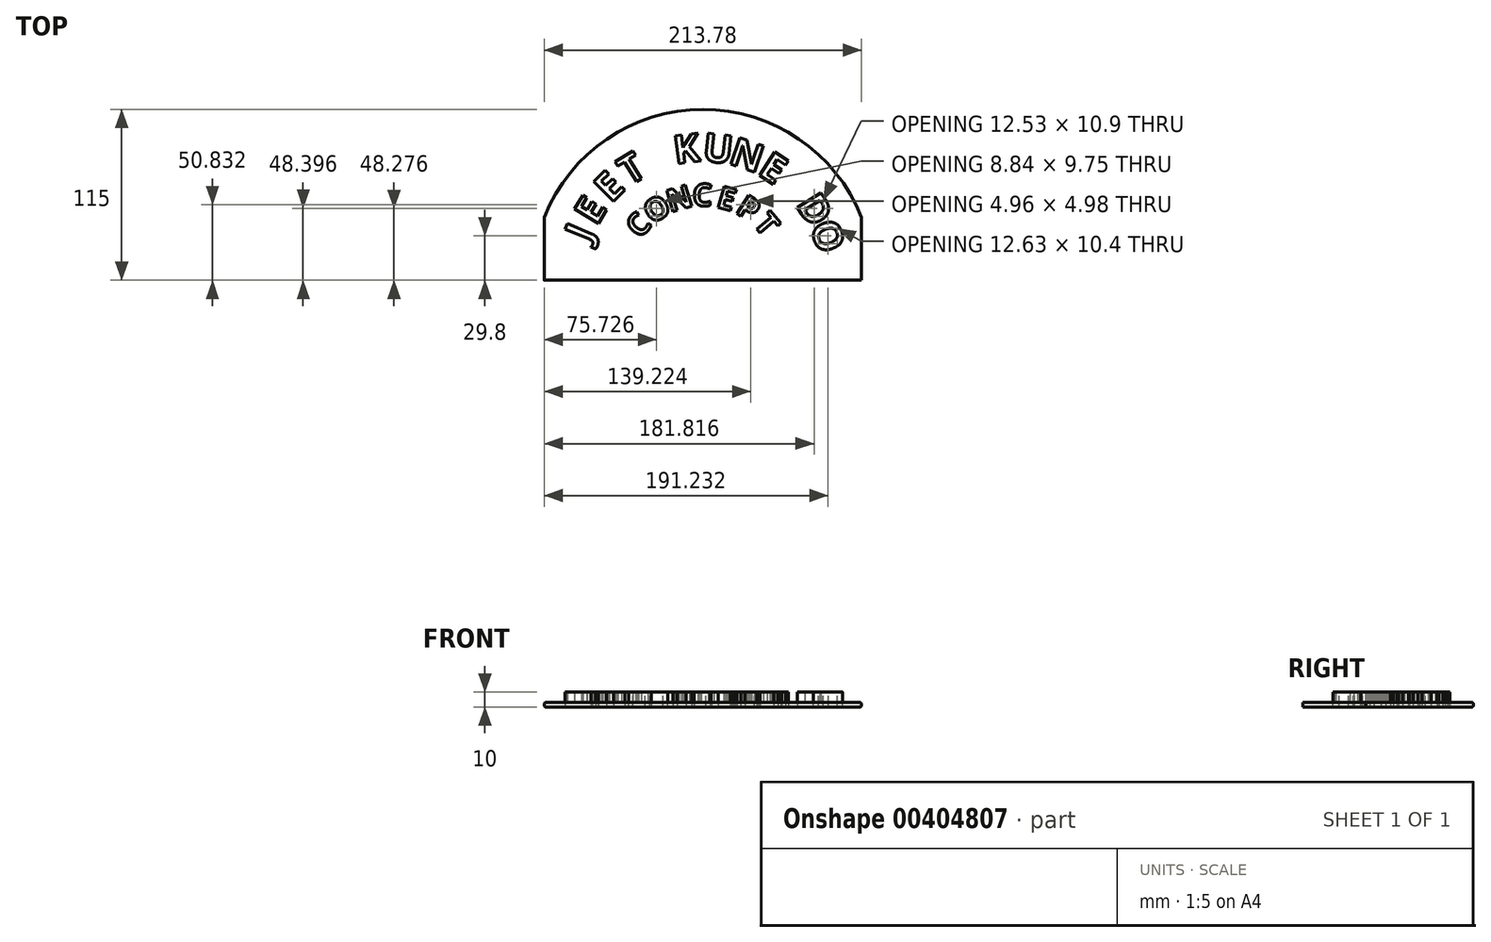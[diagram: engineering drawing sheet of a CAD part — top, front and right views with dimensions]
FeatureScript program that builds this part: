
annotation { "Feature Type Name" : "Feature", "Feature Type Description" : "" }
export const myFeature = defineFeature(function(context is Context, id is Id, definition is map)
    precondition{}
    {
        {
            var Q0;
            Q0=qCreatedBy(makeId("Top.planeOp"),FACE);
            var sketch = newSketch(context, id + "F0", { "sketchPlane" : qUnion([Q0])});
            skCircle(sketch, "E0.cCircle", {"center": v(0, 0) * mm, "radius": 80 * mm, "construction": true});
            skLineSegment(sketch, "E0.0", {"start": v(80.5, 0) * mm, "end": v(78.49, -17.91) * mm, "construction": true});
            skLineSegment(sketch, "E0.1", {"start": v(78.49, -17.91) * mm, "end": v(72.53, -34.93) * mm, "construction": true});
            skLineSegment(sketch, "E0.2", {"start": v(72.53, -34.93) * mm, "end": v(62.94, -50.2) * mm, "construction": true});
            skLineSegment(sketch, "E0.3", {"start": v(62.94, -50.2) * mm, "end": v(50.2, -62.94) * mm, "construction": true});
            skLineSegment(sketch, "E0.4", {"start": v(50.2, -62.94) * mm, "end": v(34.93, -72.53) * mm, "construction": true});
            skLineSegment(sketch, "E0.5", {"start": v(34.93, -72.53) * mm, "end": v(17.91, -78.49) * mm, "construction": true});
            skLineSegment(sketch, "E0.6", {"start": v(17.91, -78.49) * mm, "end": v(0, -80.5) * mm, "construction": true});
            skLineSegment(sketch, "E0.7", {"start": v(0, -80.5) * mm, "end": v(-17.91, -78.49) * mm, "construction": true});
            skLineSegment(sketch, "E0.8", {"start": v(-17.91, -78.49) * mm, "end": v(-34.93, -72.53) * mm, "construction": true});
            skLineSegment(sketch, "E0.9", {"start": v(-34.93, -72.53) * mm, "end": v(-50.2, -62.94) * mm, "construction": true});
            skLineSegment(sketch, "E0.10", {"start": v(-50.2, -62.94) * mm, "end": v(-62.94, -50.2) * mm, "construction": true});
            skLineSegment(sketch, "E0.11", {"start": v(-62.94, -50.2) * mm, "end": v(-72.53, -34.93) * mm, "construction": true});
            skLineSegment(sketch, "E0.12", {"start": v(-72.53, -34.93) * mm, "end": v(-78.49, -17.91) * mm, "construction": true});
            skLineSegment(sketch, "E0.13", {"start": v(-78.49, -17.91) * mm, "end": v(-80.5, 0) * mm, "construction": true});
            skLineSegment(sketch, "E0.14", {"start": v(-80.5, 0) * mm, "end": v(-78.49, 17.91) * mm, "construction": true});
            skLineSegment(sketch, "E0.15", {"start": v(-78.49, 17.91) * mm, "end": v(-72.53, 34.93) * mm, "construction": true});
            skLineSegment(sketch, "E0.16", {"start": v(-72.53, 34.93) * mm, "end": v(-62.94, 50.2) * mm, "construction": true});
            skLineSegment(sketch, "E0.17", {"start": v(-62.94, 50.2) * mm, "end": v(-50.2, 62.94) * mm, "construction": true});
            skLineSegment(sketch, "E0.18", {"start": v(-50.2, 62.94) * mm, "end": v(-34.93, 72.53) * mm, "construction": true});
            skLineSegment(sketch, "E0.19", {"start": v(-34.93, 72.53) * mm, "end": v(-17.91, 78.49) * mm, "construction": true});
            skLineSegment(sketch, "E0.20", {"start": v(-17.91, 78.49) * mm, "end": v(0, 80.5) * mm, "construction": true});
            skLineSegment(sketch, "E0.21", {"start": v(0, 80.5) * mm, "end": v(17.91, 78.49) * mm, "construction": true});
            skLineSegment(sketch, "E0.22", {"start": v(17.91, 78.49) * mm, "end": v(34.93, 72.53) * mm, "construction": true});
            skLineSegment(sketch, "E0.23", {"start": v(34.93, 72.53) * mm, "end": v(50.2, 62.94) * mm, "construction": true});
            skLineSegment(sketch, "E0.24", {"start": v(50.2, 62.94) * mm, "end": v(62.94, 50.2) * mm, "construction": true});
            skLineSegment(sketch, "E0.25", {"start": v(62.94, 50.2) * mm, "end": v(72.53, 34.93) * mm, "construction": true});
            skLineSegment(sketch, "E0.26", {"start": v(72.53, 34.93) * mm, "end": v(78.49, 17.91) * mm, "construction": true});
            skLineSegment(sketch, "E0.27", {"start": v(78.49, 17.91) * mm, "end": v(80.5, 0) * mm, "construction": true});
            skText(sketch, "E1", { "text": "J", "fontName": "OpenSans-Bold.ttf"});
            skText(sketch, "E2", { "text": "E", "fontName": "OpenSans-Bold.ttf"});
            skText(sketch, "E3", { "text": "E", "fontName": "OpenSans-Bold.ttf"});
            skText(sketch, "E4", { "text": "T", "fontName": "OpenSans-Bold.ttf"});
            skText(sketch, "E5", { "text": "K", "fontName": "OpenSans-Bold.ttf"});
            skText(sketch, "E6", { "text": "U", "fontName": "OpenSans-Bold.ttf"});
            skText(sketch, "E7", { "text": "N", "fontName": "OpenSans-Bold.ttf"});
            skText(sketch, "E8", { "text": "E", "fontName": "OpenSans-Bold.ttf"});
            skText(sketch, "E9", { "text": "D", "fontName": "OpenSans-Bold.ttf"});
            skCircle(sketch, "E10.cCircle", {"center": v(0, 0) * mm, "radius": 50 * mm, "construction": true});
            skLineSegment(sketch, "E10.0", {"start": v(50.51, 0) * mm, "end": v(48.47, -14.23) * mm, "construction": true});
            skLineSegment(sketch, "E10.1", {"start": v(48.47, -14.23) * mm, "end": v(42.5, -27.31) * mm, "construction": true});
            skLineSegment(sketch, "E10.2", {"start": v(42.5, -27.31) * mm, "end": v(33.08, -38.18) * mm, "construction": true});
            skLineSegment(sketch, "E10.3", {"start": v(33.08, -38.18) * mm, "end": v(20.98, -45.95) * mm, "construction": true});
            skLineSegment(sketch, "E10.4", {"start": v(20.98, -45.95) * mm, "end": v(7.19, -50) * mm, "construction": true});
            skLineSegment(sketch, "E10.5", {"start": v(7.19, -50) * mm, "end": v(-7.19, -50) * mm, "construction": true});
            skLineSegment(sketch, "E10.6", {"start": v(-7.19, -50) * mm, "end": v(-20.98, -45.95) * mm, "construction": true});
            skLineSegment(sketch, "E10.7", {"start": v(-20.98, -45.95) * mm, "end": v(-33.08, -38.18) * mm, "construction": true});
            skLineSegment(sketch, "E10.8", {"start": v(-33.08, -38.18) * mm, "end": v(-42.5, -27.31) * mm, "construction": true});
            skLineSegment(sketch, "E10.9", {"start": v(-42.5, -27.31) * mm, "end": v(-48.47, -14.23) * mm, "construction": true});
            skLineSegment(sketch, "E10.10", {"start": v(-48.47, -14.23) * mm, "end": v(-50.51, 0) * mm, "construction": true});
            skLineSegment(sketch, "E10.11", {"start": v(-50.51, 0) * mm, "end": v(-48.47, 14.23) * mm, "construction": true});
            skLineSegment(sketch, "E10.12", {"start": v(-48.47, 14.23) * mm, "end": v(-42.5, 27.31) * mm, "construction": true});
            skLineSegment(sketch, "E10.13", {"start": v(-42.5, 27.31) * mm, "end": v(-33.08, 38.18) * mm});
            skLineSegment(sketch, "E10.14", {"start": v(-33.08, 38.18) * mm, "end": v(-20.98, 45.95) * mm});
            skLineSegment(sketch, "E10.15", {"start": v(-20.98, 45.95) * mm, "end": v(-7.19, 50) * mm});
            skLineSegment(sketch, "E10.16", {"start": v(-7.19, 50) * mm, "end": v(7.19, 50) * mm});
            skLineSegment(sketch, "E10.17", {"start": v(7.19, 50) * mm, "end": v(20.98, 45.95) * mm});
            skLineSegment(sketch, "E10.18", {"start": v(20.98, 45.95) * mm, "end": v(33.08, 38.18) * mm});
            skLineSegment(sketch, "E10.19", {"start": v(33.08, 38.18) * mm, "end": v(42.5, 27.31) * mm});
            skLineSegment(sketch, "E10.20", {"start": v(42.5, 27.31) * mm, "end": v(48.47, 14.23) * mm, "construction": true});
            skLineSegment(sketch, "E10.21", {"start": v(48.47, 14.23) * mm, "end": v(50.51, 0) * mm, "construction": true});
            skPoint(sketch, "E10.0.midPoint", {"position": v(49.5, -7.12) * mm});
            skText(sketch, "E11", { "text": "C", "fontName": "OpenSans-Bold.ttf"});
            skText(sketch, "E12", { "text": "O", "fontName": "OpenSans-Bold.ttf"});
            skText(sketch, "E13", { "text": "N", "fontName": "OpenSans-Bold.ttf"});
            skText(sketch, "E14", { "text": "C", "fontName": "OpenSans-Bold.ttf"});
            skText(sketch, "E15", { "text": "E", "fontName": "OpenSans-Bold.ttf"});
            skText(sketch, "E16", { "text": "P", "fontName": "OpenSans-Bold.ttf"});
            skText(sketch, "E17", { "text": "T", "fontName": "OpenSans-Bold.ttf"});
            skText(sketch, "E18", { "text": "O", "fontName": "OpenSans-Bold.ttf"});
            const initialGuessF0  = {"E1": [-0.07634, 0.02495, 0.38607, 0.92247, 0.019], "E2": [-0.07158, 0.03616, 0.51504, 0.85717, 0.019], "E3": [-0.06185, 0.05129, 0.7071, 0.7071, 0.019], "E4": [-0.04954, 0.06338, 0.84805, 0.52992, 0.019], "E5": [-0.0185, 0.07832, 0.99255, 0.12187, 0.019], "E6": [-0.0007, 0.08055, 0.99415, -0.108, 0.019], "E7": [0.0166, 0.0789, 0.94552, -0.32557, 0.019], "E8": [0.0363, 0.0718, 0.83867, -0.54464, 0.019], "E9": [0.06247, 0.0509, 0.53494, -0.8449, 0.019], "E11": [-0.04239, 0.02754, 0.66193, 0.74957, 0.015], "E12": [-0.03404, 0.0375, 0.83762, 0.54625, 0.015], "E13": [-0.02195, 0.04563, 0.95832, 0.28569, 0.015], "E14": [-0.00695, 0.05, 1, 0, 0.015], "E15": [0.00842, 0.0496, 0.96126, -0.27564, 0.015], "E16": [0.02136, 0.04572, 0.84028, -0.54215, 0.015], "E17": [0.0336, 0.03771, 0.6448, -0.76436, 0.015], "E18": [0.07182, 0.03635, 0.34857, -0.93728, 0.019]};
            skSetInitialGuess(sketch, initialGuessF0);
            skSolve(sketch);
        }
        {
            var Q0;
            Q0 = qSketchRegion(id + "F0", true);
            extrude(context, id + "F1", {"entities" : qUnion([Q0]), "depth" : 10 * mm});
        }
        {
            var Q0;
            Q0=qCreatedBy(makeId("Top.planeOp"),FACE);
            var sketch = newSketch(context, id + "F2", { "sketchPlane" : qUnion([Q0])});
            skCircle(sketch, "E19", {"center": v(0, 0) * mm, "radius": 115 * mm});
            skLineSegment(sketch, "E20.bottom", {"start": v(0, 0) * mm, "end": v(106.9, 0) * mm});
            skLineSegment(sketch, "E20.top", {"start": v(0, 42.41) * mm, "end": v(106.9, 42.41) * mm});
            skLineSegment(sketch, "E20.left", {"start": v(0, 0) * mm, "end": v(0, 42.41) * mm});
            skLineSegment(sketch, "E20.right", {"start": v(106.9, 0) * mm, "end": v(106.9, 42.41) * mm});
            skLineSegment(sketch, "E21.MirrorCS", {"start": v(-106.9, 0) * mm, "end": v(-106.9, 42.41) * mm});
            skLineSegment(sketch, "E22.MirrorCS", {"start": v(0, 0) * mm, "end": v(-106.9, 0) * mm});
            skSolve(sketch);
        }
        {
            var Q0;
            {var subQ1=sQuery(id+"F2.wireOp",EDGE,"E20.top");Q0=makeQuery(id+"F2.imprint","IMPRINT",FACE,{"disambiguationData":[TD([[makeQuery(id+"F2.imprint","IMPRINT",EDGE,{"derivedFrom":subQ1}),1.0]])]});}
            var Q1;
            Q1=makeQuery(id+"F2.imprint","IMPRINT",FACE,{"disambiguationData":[TD([[makeQuery(id+"F2.imprint","IMPRINT",EDGE,{"derivedFrom":sQuery(id+"F2.wireOp",EDGE,"E20.bottom")}),1.0]])]});
            extrude(context, id + "F3", {"entities" : qUnion([Q0, Q1]), "depth" : 3 * mm});
        }
        {
            var Q0;
            Q0=makeQuery(id+"F3.opExtrude","CAP_EDGE",EDGE,{"disambiguationData":[OSD([sQuery(id+"F2.wireOp",EDGE,"E19")])],"isStart":false});
            var Q1;
            Q1=makeQuery(id+"F3.opExtrude","CAP_EDGE",EDGE,{"disambiguationData":[OSD([sQuery(id+"F2.wireOp",EDGE,"E21.MirrorCS")])],"isStart":false});
            var Q2;
            Q2=makeQuery(id+"F3.opExtrude","CAP_EDGE",EDGE,{"disambiguationData":[OSD([sQuery(id+"F2.wireOp",EDGE,"E20.right")])],"isStart":false});
            fillet(context, id + "F4", {"entities" : qUnion([Q0, Q1, Q2]), "radius" : 1 * mm, "tangentPropagation" : true, "allowEdgeOverflow" : false});
        }
        {
            var Q0;
            Q0=makeQuery(id+"F3.opExtrude","CAP_EDGE",EDGE,{"disambiguationData":[OSD([sQuery(id+"F2.wireOp",EDGE,"E19")])],"isStart":true});
            var Q1;
            Q1=makeQuery(id+"F3.opExtrude","CAP_EDGE",EDGE,{"disambiguationData":[OSD([sQuery(id+"F2.wireOp",EDGE,"E21.MirrorCS")])],"isStart":true});
            var Q2;
            Q2=makeQuery(id+"F3.opExtrude","CAP_EDGE",EDGE,{"disambiguationData":[OSD([sQuery(id+"F2.wireOp",EDGE,"E20.right")])],"isStart":true});
            fillet(context, id + "F5", {"entities" : qUnion([Q0, Q1, Q2]), "radius" : 1 * mm, "tangentPropagation" : true, "allowEdgeOverflow" : false});
        }
    });
